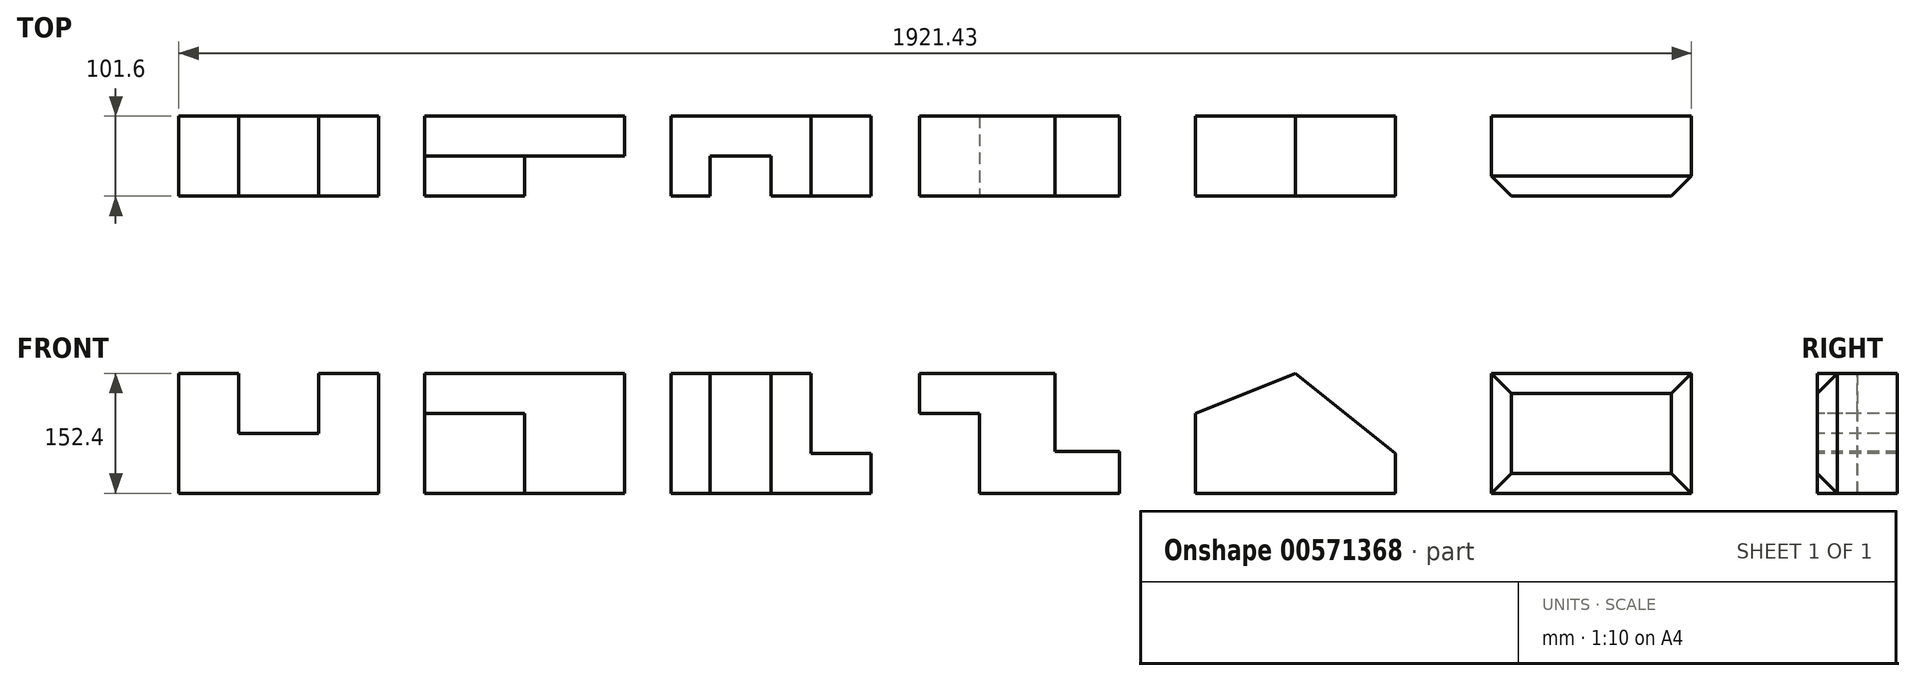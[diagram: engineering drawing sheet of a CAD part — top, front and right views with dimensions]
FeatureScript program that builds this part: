
annotation { "Feature Type Name" : "Feature", "Feature Type Description" : "" }
export const myFeature = defineFeature(function(context is Context, id is Id, definition is map)
    precondition{}
    {
        {
            var Q0;
            Q0=qCreatedBy(makeId("Front.planeOp"),FACE);
            var sketch = newSketch(context, id + "F0", { "sketchPlane" : qUnion([Q0])});
            skLineSegment(sketch, "E0", {"start": v(0, 0) * mm, "end": v(254, 0) * mm});
            skLineSegment(sketch, "E1", {"start": v(254, 0) * mm, "end": v(254, 152.4) * mm});
            skLineSegment(sketch, "E2", {"start": v(254, 152.4) * mm, "end": v(177.8, 152.4) * mm});
            skLineSegment(sketch, "E3", {"start": v(177.8, 152.4) * mm, "end": v(177.8, 76.2) * mm});
            skLineSegment(sketch, "E4", {"start": v(177.8, 76.2) * mm, "end": v(76.2, 76.2) * mm});
            skLineSegment(sketch, "E5", {"start": v(76.2, 76.2) * mm, "end": v(76.2, 152.4) * mm});
            skLineSegment(sketch, "E6", {"start": v(76.2, 152.4) * mm, "end": v(0, 152.4) * mm});
            skLineSegment(sketch, "E7", {"start": v(0, 152.4) * mm, "end": v(0, 0) * mm});
            skSolve(sketch);
        }
        {
            var Q0;
            Q0=makeQuery(id+"F0.imprint","IMPRINT",FACE,{"disambiguationData":[TD([[makeQuery(id+"F0.imprint","IMPRINT",EDGE,{"derivedFrom":sQuery(id+"F0.wireOp",EDGE,"E0")}),1.0]])]});
            extrude(context, id + "F1", {"entities" : qUnion([Q0]), "oppositeDirection" : true, "depth" : 101.6 * mm, "offsetDistance" : 25.4 * mm});
        }
        {
            var Q0;
            Q0=makeQuery(id+"F1.opExtrude","CAP_FACE",FACE,{"disambiguationData":[OSD([sQuery(id+"F0.wireOp",EDGE,"E0"),sQuery(id+"F0.wireOp",EDGE,"E1"),sQuery(id+"F0.wireOp",EDGE,"E2"),sQuery(id+"F0.wireOp",EDGE,"E3"),sQuery(id+"F0.wireOp",EDGE,"E4"),sQuery(id+"F0.wireOp",EDGE,"E5"),sQuery(id+"F0.wireOp",EDGE,"E6"),sQuery(id+"F0.wireOp",EDGE,"E7")])],"isStart":true});
            var sketch = newSketch(context, id + "F2", { "sketchPlane" : qUnion([Q0])});
            skLineSegment(sketch, "E8", {"start": v(312.27, 0) * mm, "end": v(566.27, 0) * mm});
            skLineSegment(sketch, "E9", {"start": v(312.27, 0) * mm, "end": v(312.27, 152.4) * mm});
            skLineSegment(sketch, "E10", {"start": v(312.27, 152.4) * mm, "end": v(566.27, 152.4) * mm});
            skLineSegment(sketch, "E11", {"start": v(566.27, 152.4) * mm, "end": v(566.27, 0) * mm});
            skSolve(sketch);
        }
        {
            var Q0;
            Q0 = qSketchRegion(id + "F2", true);
            extrude(context, id + "F3", {"entities" : qUnion([Q0]), "oppositeDirection" : true, "depth" : 101.6 * mm, "offsetDistance" : 25.4 * mm});
        }
        {
            var Q0;
            Q0=makeQuery(id+"F3.opExtrude","SWEPT_FACE",FACE,{"disambiguationData":[OSD([sQuery(id+"F2.wireOp",EDGE,"E10")])]});
            var sketch = newSketch(context, id + "F4", { "sketchPlane" : qUnion([Q0])});
            skLineSegment(sketch, "E12", {"start": v(439.27, 0) * mm, "end": v(439.27, 50.8) * mm});
            skLineSegment(sketch, "E13", {"start": v(439.27, 50.8) * mm, "end": v(566.27, 50.8) * mm});
            skLineSegment(sketch, "E14", {"start": v(566.27, 50.8) * mm, "end": v(566.27, 0) * mm});
            skLineSegment(sketch, "E15", {"start": v(566.27, 0) * mm, "end": v(439.27, 0) * mm});
            skSolve(sketch);
        }
        {
            var Q0;
            Q0=makeQuery(id+"F4.imprint","IMPRINT",FACE,{"disambiguationData":[TD([[makeQuery(id+"F4.imprint","IMPRINT",EDGE,{"derivedFrom":sQuery(id+"F4.wireOp",EDGE,"E12")}),-1.0]])]});
            extrude(context, id + "F5", {"entities" : qUnion([Q0]), "operationType" : NewBodyOperationType.REMOVE, "oppositeDirection" : true, "depth" : 152.4 * mm, "offsetDistance" : 25.4 * mm});
        }
        {
            var Q0;
            Q0=makeQuery(id+"F1.opExtrude","CAP_FACE",FACE,{"disambiguationData":[OSD([sQuery(id+"F0.wireOp",EDGE,"E0"),sQuery(id+"F0.wireOp",EDGE,"E1"),sQuery(id+"F0.wireOp",EDGE,"E2"),sQuery(id+"F0.wireOp",EDGE,"E3"),sQuery(id+"F0.wireOp",EDGE,"E4"),sQuery(id+"F0.wireOp",EDGE,"E5"),sQuery(id+"F0.wireOp",EDGE,"E6"),sQuery(id+"F0.wireOp",EDGE,"E7")])],"isStart":true});
            var sketch = newSketch(context, id + "F6", { "sketchPlane" : qUnion([Q0])});
            skLineSegment(sketch, "E16", {"start": v(625.55, 0) * mm, "end": v(879.55, 0) * mm});
            skLineSegment(sketch, "E17", {"start": v(625.55, 0) * mm, "end": v(625.55, 152.4) * mm});
            skLineSegment(sketch, "E18", {"start": v(625.55, 152.4) * mm, "end": v(879.55, 152.4) * mm});
            skLineSegment(sketch, "E19", {"start": v(879.55, 152.4) * mm, "end": v(879.55, 0) * mm});
            skSolve(sketch);
        }
        {
            var Q0;
            Q0=makeQuery(id+"F3.opExtrude","SWEPT_FACE",FACE,{"disambiguationData":[OSD([sQuery(id+"F2.wireOp",EDGE,"E10")])]});
            var sketch = newSketch(context, id + "F7", { "sketchPlane" : qUnion([Q0])});
            skLineSegment(sketch, "E20", {"start": v(312.27, 0) * mm, "end": v(312.27, 50.8) * mm});
            skLineSegment(sketch, "E21", {"start": v(312.27, 50.8) * mm, "end": v(439.27, 50.8) * mm});
            skLineSegment(sketch, "E22", {"start": v(439.27, 50.8) * mm, "end": v(439.27, 0) * mm});
            skLineSegment(sketch, "E23", {"start": v(439.27, 0) * mm, "end": v(312.27, 0) * mm});
            skSolve(sketch);
        }
        {
            var Q0;
            Q0 = qSketchRegion(id + "F7", true);
            extrude(context, id + "F8", {"entities" : qUnion([Q0]), "operationType" : NewBodyOperationType.REMOVE, "oppositeDirection" : true, "depth" : 50.8 * mm, "offsetDistance" : 25.4 * mm});
        }
        {
            var Q0;
            Q0 = qSketchRegion(id + "F6", true);
            extrude(context, id + "F9", {"entities" : qUnion([Q0]), "oppositeDirection" : true, "depth" : 101.6 * mm, "offsetDistance" : 25.4 * mm});
        }
        {
            var Q0;
            Q0=makeQuery(id+"F9.opExtrude","SWEPT_FACE",FACE,{"disambiguationData":[OSD([sQuery(id+"F6.wireOp",EDGE,"E18")])]});
            var sketch = newSketch(context, id + "F10", { "sketchPlane" : qUnion([Q0])});
            skLineSegment(sketch, "E24", {"start": v(803.35, 101.6) * mm, "end": v(803.35, 0) * mm});
            skLineSegment(sketch, "E25", {"start": v(803.35, 0) * mm, "end": v(879.55, 0) * mm});
            skLineSegment(sketch, "E26", {"start": v(879.55, 0) * mm, "end": v(879.55, 101.6) * mm});
            skLineSegment(sketch, "E27", {"start": v(879.55, 101.6) * mm, "end": v(803.35, 101.6) * mm});
            skSolve(sketch);
        }
        {
            var Q0;
            Q0 = qSketchRegion(id + "F10", true);
            extrude(context, id + "F11", {"entities" : qUnion([Q0]), "operationType" : NewBodyOperationType.REMOVE, "oppositeDirection" : true, "depth" : 101.6 * mm, "offsetDistance" : 25.4 * mm});
        }
        {
            var Q0;
            Q0=makeQuery(id+"F9.opExtrude","CAP_FACE",FACE,{"disambiguationData":[OSD([sQuery(id+"F6.wireOp",EDGE,"E16"),sQuery(id+"F6.wireOp",EDGE,"E17"),sQuery(id+"F6.wireOp",EDGE,"E18"),sQuery(id+"F6.wireOp",EDGE,"E19")])],"isStart":true});
            var sketch = newSketch(context, id + "F12", { "sketchPlane" : qUnion([Q0])});
            skLineSegment(sketch, "E28", {"start": v(625.55, 152.4) * mm, "end": v(675.04, 152.4) * mm});
            skLineSegment(sketch, "E29", {"start": v(675.04, 152.4) * mm, "end": v(675.04, 0) * mm});
            skLineSegment(sketch, "E30", {"start": v(675.04, 0) * mm, "end": v(625.55, 0) * mm});
            skLineSegment(sketch, "E31", {"start": v(625.55, 0) * mm, "end": v(625.55, 152.4) * mm});
            skLineSegment(sketch, "E32", {"start": v(625.55, 152.4) * mm, "end": v(625.55, 0) * mm});
            skLineSegment(sketch, "E33", {"start": v(803.35, 152.4) * mm, "end": v(752.55, 152.4) * mm});
            skLineSegment(sketch, "E34", {"start": v(752.55, 152.4) * mm, "end": v(752.55, 0) * mm});
            skLineSegment(sketch, "E35", {"start": v(752.55, 0) * mm, "end": v(803.35, 0) * mm});
            skLineSegment(sketch, "E36", {"start": v(803.35, 0) * mm, "end": v(803.35, 152.4) * mm});
            skLineSegment(sketch, "E37.bottom", {"start": v(675.04, 152.4) * mm, "end": v(752.55, 152.4) * mm});
            skLineSegment(sketch, "E37.top", {"start": v(675.04, 152.4) * mm, "end": v(752.55, 152.4) * mm});
            skLineSegment(sketch, "E37.left", {"start": v(675.04, 152.4) * mm, "end": v(675.04, 152.4) * mm});
            skLineSegment(sketch, "E37.right", {"start": v(752.55, 152.4) * mm, "end": v(752.55, 152.4) * mm});
            skLineSegment(sketch, "E38.bottom", {"start": v(752.55, 0) * mm, "end": v(675.04, 0) * mm});
            skLineSegment(sketch, "E38.top", {"start": v(752.55, 0) * mm, "end": v(675.04, 0) * mm});
            skLineSegment(sketch, "E38.left", {"start": v(752.55, 0) * mm, "end": v(752.55, 0) * mm});
            skLineSegment(sketch, "E38.right", {"start": v(675.04, 0) * mm, "end": v(675.04, 0) * mm});
            skSolve(sketch);
        }
        {
            var Q0;
            Q0=makeQuery(id+"F12.imprint","IMPRINT",FACE,{"disambiguationData":[TD([[makeQuery(id+"F12.imprint","IMPRINT",EDGE,{"derivedFrom":sQuery(id+"F12.wireOp",EDGE,"E29")}),1.0]])]});
            extrude(context, id + "F13", {"entities" : qUnion([Q0]), "operationType" : NewBodyOperationType.REMOVE, "oppositeDirection" : true, "depth" : 50.8 * mm, "offsetDistance" : 25.4 * mm});
        }
        {
            var Q0;
            {var subQ1=sQuery(id+"F6.wireOp",EDGE,"E19");var subQ2=sQuery(id+"F6.wireOp",EDGE,"E18");var subQ3=sQuery(id+"F6.wireOp",EDGE,"E16");Q0=makeQuery(id+"F13.boolean.opBoolean","SPLIT",FACE,{"disambiguationData":[TD([makeQuery(id+"F9.opExtrude","SWEPT_FACE",FACE,{"disambiguationData":[OSD([subQ1])]})])],"derivedFrom":makeQuery(id+"F9.opExtrude","CAP_FACE",FACE,{"disambiguationData":[OSD([subQ3,sQuery(id+"F6.wireOp",EDGE,"E17"),subQ2,subQ1])],"isStart":true})});}
            var sketch = newSketch(context, id + "F14", { "sketchPlane" : qUnion([Q0])});
            skLineSegment(sketch, "E39", {"start": v(940.89, 0) * mm, "end": v(940.89, 152.4) * mm});
            skLineSegment(sketch, "E40", {"start": v(940.89, 152.4) * mm, "end": v(1194.89, 152.4) * mm});
            skLineSegment(sketch, "E41", {"start": v(1194.89, 152.4) * mm, "end": v(1194.89, 0) * mm});
            skLineSegment(sketch, "E42", {"start": v(1194.89, 0) * mm, "end": v(940.89, 0) * mm});
            skSolve(sketch);
        }
        {
            var Q0;
            Q0 = qSketchRegion(id + "F14", true);
            extrude(context, id + "F15", {"entities" : qUnion([Q0]), "oppositeDirection" : true, "depth" : 101.6 * mm, "offsetDistance" : 25.4 * mm});
        }
        {
            var Q0;
            Q0=makeQuery(id+"F15.opExtrude","CAP_FACE",FACE,{"disambiguationData":[OSD([sQuery(id+"F14.wireOp",EDGE,"E39"),sQuery(id+"F14.wireOp",EDGE,"E40"),sQuery(id+"F14.wireOp",EDGE,"E41"),sQuery(id+"F14.wireOp",EDGE,"E42")])],"isStart":true});
            var sketch = newSketch(context, id + "F16", { "sketchPlane" : qUnion([Q0])});
            skLineSegment(sketch, "E43", {"start": v(940.89, 101.6) * mm, "end": v(1017.09, 101.6) * mm});
            skLineSegment(sketch, "E44", {"start": v(1017.09, 101.6) * mm, "end": v(1017.09, 0) * mm});
            skLineSegment(sketch, "E45", {"start": v(1017.09, 0) * mm, "end": v(940.89, 0) * mm});
            skLineSegment(sketch, "E46", {"start": v(940.89, 0) * mm, "end": v(940.89, 101.6) * mm});
            skSolve(sketch);
        }
        {
            var Q0;
            Q0 = qSketchRegion(id + "F16", true);
            extrude(context, id + "F17", {"entities" : qUnion([Q0]), "operationType" : NewBodyOperationType.REMOVE, "oppositeDirection" : true, "depth" : 101.6 * mm, "offsetDistance" : 25.4 * mm});
        }
        {
            var Q0;
            Q0=makeQuery(id+"F15.opExtrude","CAP_FACE",FACE,{"disambiguationData":[OSD([sQuery(id+"F14.wireOp",EDGE,"E39"),sQuery(id+"F14.wireOp",EDGE,"E40"),sQuery(id+"F14.wireOp",EDGE,"E41"),sQuery(id+"F14.wireOp",EDGE,"E42")])],"isStart":true});
            var sketch = newSketch(context, id + "F18", { "sketchPlane" : qUnion([Q0])});
            skLineSegment(sketch, "E47", {"start": v(1112.78, 152.4) * mm, "end": v(1112.78, 53.08) * mm});
            skLineSegment(sketch, "E48", {"start": v(1112.78, 53.08) * mm, "end": v(1194.89, 53.08) * mm});
            skLineSegment(sketch, "E49", {"start": v(1194.89, 53.08) * mm, "end": v(1194.89, 152.4) * mm});
            skLineSegment(sketch, "E50", {"start": v(1194.89, 152.4) * mm, "end": v(1112.78, 152.4) * mm});
            skSolve(sketch);
        }
        {
            var Q0;
            Q0 = qSketchRegion(id + "F18", true);
            extrude(context, id + "F19", {"entities" : qUnion([Q0]), "operationType" : NewBodyOperationType.REMOVE, "oppositeDirection" : true, "depth" : 101.6 * mm, "offsetDistance" : 25.4 * mm});
        }
        {
            var Q0;
            Q0=makeQuery(id+"F15.opExtrude","CAP_FACE",FACE,{"disambiguationData":[OSD([sQuery(id+"F14.wireOp",EDGE,"E39"),sQuery(id+"F14.wireOp",EDGE,"E40"),sQuery(id+"F14.wireOp",EDGE,"E41"),sQuery(id+"F14.wireOp",EDGE,"E42")])],"isStart":true});
            var sketch = newSketch(context, id + "F20", { "sketchPlane" : qUnion([Q0])});
            skLineSegment(sketch, "E51", {"start": v(1291.53, 0) * mm, "end": v(1545.53, 0) * mm});
            skLineSegment(sketch, "E52", {"start": v(1545.53, 0) * mm, "end": v(1545.53, 152.4) * mm});
            skLineSegment(sketch, "E53", {"start": v(1545.53, 152.4) * mm, "end": v(1291.53, 152.4) * mm});
            skLineSegment(sketch, "E54", {"start": v(1291.53, 152.4) * mm, "end": v(1291.53, 0) * mm});
            skSolve(sketch);
        }
        {
            var Q0;
            Q0 = qSketchRegion(id + "F20", true);
            extrude(context, id + "F21", {"entities" : qUnion([Q0]), "oppositeDirection" : true, "depth" : 101.6 * mm, "offsetDistance" : 25.4 * mm});
        }
        {
            var Q0;
            Q0=makeQuery(id+"F21.opExtrude","CAP_FACE",FACE,{"disambiguationData":[OSD([sQuery(id+"F20.wireOp",EDGE,"E51"),sQuery(id+"F20.wireOp",EDGE,"E52"),sQuery(id+"F20.wireOp",EDGE,"E53"),sQuery(id+"F20.wireOp",EDGE,"E54")])],"isStart":true});
            var sketch = newSketch(context, id + "F22", { "sketchPlane" : qUnion([Q0])});
            skLineSegment(sketch, "E55", {"start": v(1291.53, 101.6) * mm, "end": v(1291.53, 152.4) * mm});
            skLineSegment(sketch, "E56", {"start": v(1291.53, 152.4) * mm, "end": v(1418.53, 152.4) * mm});
            skLineSegment(sketch, "E57", {"start": v(1418.53, 152.4) * mm, "end": v(1291.53, 101.6) * mm});
            skSolve(sketch);
        }
        {
            var Q0;
            Q0 = qSketchRegion(id + "F22", true);
            extrude(context, id + "F23", {"entities" : qUnion([Q0]), "operationType" : NewBodyOperationType.REMOVE, "oppositeDirection" : true, "depth" : 101.6 * mm, "offsetDistance" : 25.4 * mm});
        }
        {
            var Q0;
            Q0=makeQuery(id+"F21.opExtrude","CAP_FACE",FACE,{"disambiguationData":[OSD([sQuery(id+"F20.wireOp",EDGE,"E51"),sQuery(id+"F20.wireOp",EDGE,"E52"),sQuery(id+"F20.wireOp",EDGE,"E53"),sQuery(id+"F20.wireOp",EDGE,"E54")])],"isStart":true});
            var sketch = newSketch(context, id + "F24", { "sketchPlane" : qUnion([Q0])});
            skLineSegment(sketch, "E58", {"start": v(1545.53, 50.8) * mm, "end": v(1545.53, 152.4) * mm});
            skLineSegment(sketch, "E59", {"start": v(1545.53, 152.4) * mm, "end": v(1418.53, 152.4) * mm});
            skLineSegment(sketch, "E60", {"start": v(1418.53, 152.4) * mm, "end": v(1545.53, 50.8) * mm});
            skSolve(sketch);
        }
        {
            var Q0;
            Q0 = qSketchRegion(id + "F24", true);
            extrude(context, id + "F25", {"entities" : qUnion([Q0]), "operationType" : NewBodyOperationType.REMOVE, "oppositeDirection" : true, "depth" : 101.6 * mm, "offsetDistance" : 25.4 * mm});
        }
        {
            var Q0;
            Q0=makeQuery(id+"F21.opExtrude","CAP_FACE",FACE,{"disambiguationData":[OSD([sQuery(id+"F20.wireOp",EDGE,"E51"),sQuery(id+"F20.wireOp",EDGE,"E52"),sQuery(id+"F20.wireOp",EDGE,"E53"),sQuery(id+"F20.wireOp",EDGE,"E54")])],"isStart":true});
            var sketch = newSketch(context, id + "F26", { "sketchPlane" : qUnion([Q0])});
            skLineSegment(sketch, "E61", {"start": v(1667.43, 0) * mm, "end": v(1921.43, 0) * mm});
            skLineSegment(sketch, "E62", {"start": v(1921.43, 0) * mm, "end": v(1921.43, 152.4) * mm});
            skLineSegment(sketch, "E63", {"start": v(1921.43, 152.4) * mm, "end": v(1667.43, 152.4) * mm});
            skLineSegment(sketch, "E64", {"start": v(1667.43, 152.4) * mm, "end": v(1667.43, 0) * mm});
            skSolve(sketch);
        }
        {
            var Q0;
            Q0 = qSketchRegion(id + "F26", true);
            extrude(context, id + "F27", {"entities" : qUnion([Q0]), "oppositeDirection" : true, "depth" : 101.6 * mm, "offsetDistance" : 25.4 * mm});
        }
        {
            var Q0;
            Q0=makeQuery(id+"F27.opExtrude","CAP_FACE",FACE,{"disambiguationData":[OSD([sQuery(id+"F26.wireOp",EDGE,"E61"),sQuery(id+"F26.wireOp",EDGE,"E62"),sQuery(id+"F26.wireOp",EDGE,"E63"),sQuery(id+"F26.wireOp",EDGE,"E64")])],"isStart":true});
            chamfer(context, id + "F28", {"entities" : qUnion([Q0]), "width" : 25.4 * mm, "tangentPropagation" : true});
        }
    });
